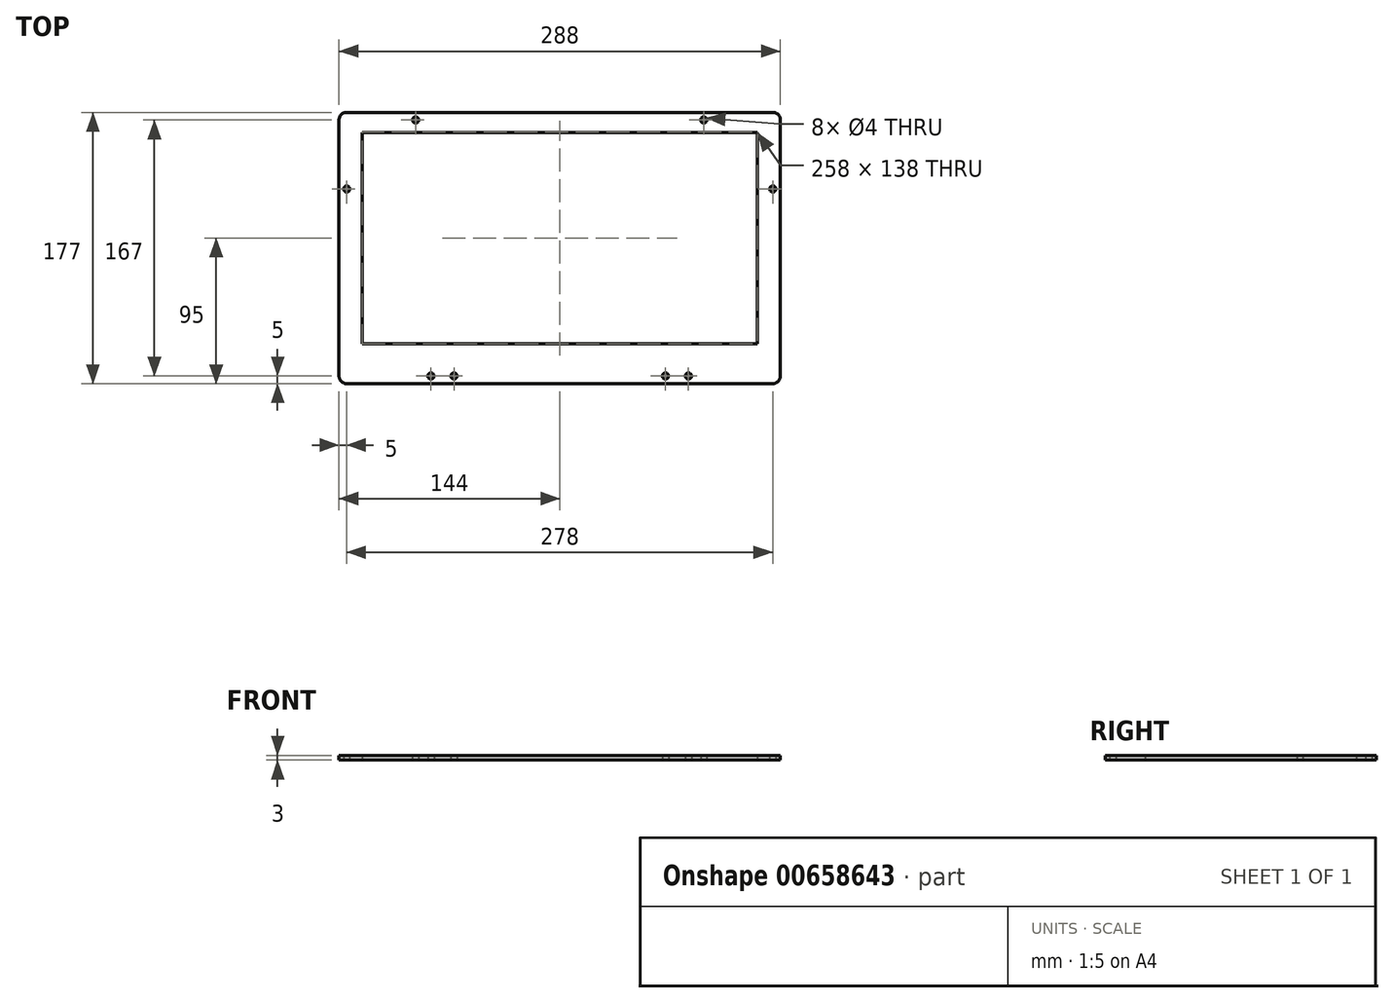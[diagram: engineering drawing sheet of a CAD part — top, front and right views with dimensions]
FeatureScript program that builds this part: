
annotation { "Feature Type Name" : "Feature", "Feature Type Description" : "" }
export const myFeature = defineFeature(function(context is Context, id is Id, definition is map)
    precondition{}
    {
        {
            var Q0;
            Q0=qCreatedBy(makeId("Top.planeOp"),FACE);
            var sketch = newSketch(context, id + "F0", { "sketchPlane" : qUnion([Q0])});
            skLineSegment(sketch, "E0.bottom", {"start": v(-144, 96) * mm, "end": v(144, 96) * mm});
            skLineSegment(sketch, "E0.top", {"start": v(-144, -81) * mm, "end": v(144, -81) * mm});
            skLineSegment(sketch, "E0.left", {"start": v(-144, 96) * mm, "end": v(-144, -81) * mm});
            skLineSegment(sketch, "E0.right", {"start": v(144, 96) * mm, "end": v(144, -81) * mm});
            skCircle(sketch, "E1", {"center": v(-94, 91) * mm, "radius": 2 * mm});
            skCircle(sketch, "E2", {"center": v(-139, 46) * mm, "radius": 2 * mm});
            skCircle(sketch, "E3", {"center": v(94, 91) * mm, "radius": 2 * mm});
            skCircle(sketch, "E4", {"center": v(139, 46) * mm, "radius": 2 * mm});
            skCircle(sketch, "E5", {"center": v(-84, -76) * mm, "radius": 2 * mm});
            skCircle(sketch, "E6", {"center": v(-69, -76) * mm, "radius": 2 * mm});
            skCircle(sketch, "E7", {"center": v(84, -76) * mm, "radius": 2 * mm});
            skCircle(sketch, "E8", {"center": v(69, -76) * mm, "radius": 2 * mm});
            skLineSegment(sketch, "E9.bottom", {"start": v(-129, 83) * mm, "end": v(129, 83) * mm});
            skLineSegment(sketch, "E9.top", {"start": v(-129, -55) * mm, "end": v(129, -55) * mm});
            skLineSegment(sketch, "E9.left", {"start": v(-129, 83) * mm, "end": v(-129, -55) * mm});
            skLineSegment(sketch, "E9.right", {"start": v(129, 83) * mm, "end": v(129, -55) * mm});
            skSolve(sketch);
        }
        {
            var Q0;
            Q0=makeQuery(id+"F0.imprint","IMPRINT",FACE,{"disambiguationData":[TD([[makeQuery(id+"F0.imprint","IMPRINT",EDGE,{"derivedFrom":sQuery(id+"F0.wireOp",EDGE,"E0.bottom")}),-1.0]])]});
            extrude(context, id + "F1", {"entities" : qUnion([Q0]), "depth" : 3 * mm, "offsetDistance" : 25 * mm});
        }
        {
            var Q0;
            Q0=makeQuery(id+"F1.opExtrude","SWEPT_EDGE",EDGE,{"disambiguationData":[OSD([sQuery(id+"F0.wireOp",EDGE,"E0.bottom"),sQuery(id+"F0.wireOp",EDGE,"E0.left")])]});
            var Q1;
            Q1=makeQuery(id+"F1.opExtrude","SWEPT_EDGE",EDGE,{"disambiguationData":[OSD([sQuery(id+"F0.wireOp",EDGE,"E0.top"),sQuery(id+"F0.wireOp",EDGE,"E0.left")])]});
            var Q2;
            Q2=makeQuery(id+"F1.opExtrude","SWEPT_EDGE",EDGE,{"disambiguationData":[OSD([sQuery(id+"F0.wireOp",EDGE,"E0.top"),sQuery(id+"F0.wireOp",EDGE,"E0.right")])]});
            var Q3;
            Q3=makeQuery(id+"F1.opExtrude","SWEPT_EDGE",EDGE,{"disambiguationData":[OSD([sQuery(id+"F0.wireOp",EDGE,"E0.bottom"),sQuery(id+"F0.wireOp",EDGE,"E0.right")])]});
            fillet(context, id + "F2", {"entities" : qUnion([Q0, Q1, Q2, Q3]), "radius" : 5 * mm, "tangentPropagation" : true, "allowEdgeOverflow" : false});
        }
    });
